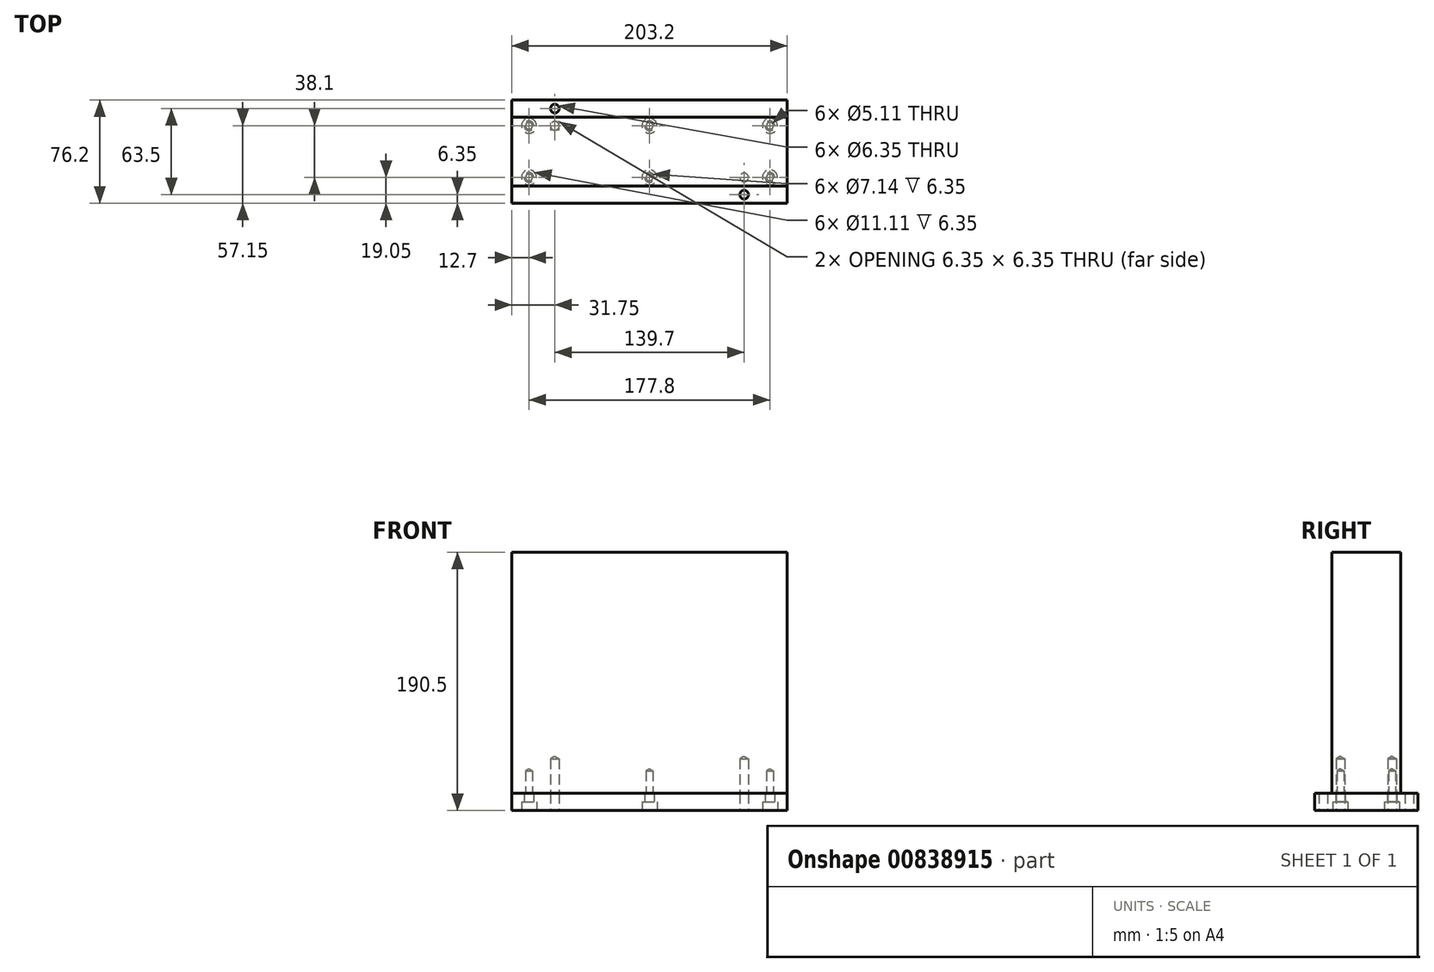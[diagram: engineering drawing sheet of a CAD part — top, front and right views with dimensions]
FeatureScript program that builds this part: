
annotation { "Feature Type Name" : "Feature", "Feature Type Description" : "" }
export const myFeature = defineFeature(function(context is Context, id is Id, definition is map)
    precondition{}
    {
        {
            var Q0;
            Q0=qCreatedBy(makeId("Top.planeOp"),FACE);
            var sketch = newSketch(context, id + "F0", { "sketchPlane" : qUnion([Q0])});
            skLineSegment(sketch, "E0.bottom", {"start": v(101.6, -38.1) * mm, "end": v(-101.6, -38.1) * mm});
            skLineSegment(sketch, "E0.top", {"start": v(101.6, 38.1) * mm, "end": v(-101.6, 38.1) * mm});
            skLineSegment(sketch, "E0.left", {"start": v(101.6, -38.1) * mm, "end": v(101.6, 38.1) * mm});
            skLineSegment(sketch, "E0.right", {"start": v(-101.6, -38.1) * mm, "end": v(-101.6, 38.1) * mm});
            skPoint(sketch, "E0.middle", {"position": v(0, 0) * mm});
            skSolve(sketch);
        }
        {
            var Q0;
            Q0=qSketchRegion(id+"F0",true);
            extrude(context, id + "F1", {"entities" : qUnion([Q0]), "depth" : 12.7 * mm, "offsetDistance" : 25.4 * mm});
        }
        {
            var Q0;
            Q0=makeQuery(id+"F1.opExtrude","CAP_FACE",FACE,{"disambiguationData":[OSD([sQuery(id+"F0.wireOp",EDGE,"E0.bottom"),sQuery(id+"F0.wireOp",EDGE,"E0.top"),sQuery(id+"F0.wireOp",EDGE,"E0.left"),sQuery(id+"F0.wireOp",EDGE,"E0.right")])],"isStart":false});
            var sketch = newSketch(context, id + "F2", { "sketchPlane" : qUnion([Q0])});
            skLineSegment(sketch, "E1.bottom", {"start": v(101.6, -25.4) * mm, "end": v(-101.6, -25.4) * mm});
            skLineSegment(sketch, "E1.top", {"start": v(101.6, 25.4) * mm, "end": v(-101.6, 25.4) * mm});
            skLineSegment(sketch, "E1.left", {"start": v(101.6, -25.4) * mm, "end": v(101.6, 25.4) * mm});
            skLineSegment(sketch, "E1.right", {"start": v(-101.6, -25.4) * mm, "end": v(-101.6, 25.4) * mm});
            skPoint(sketch, "E1.middle", {"position": v(0, 0) * mm});
            skSolve(sketch);
        }
        {
            var Q0;
            Q0=qSketchRegion(id+"F2",true);
            extrude(context, id + "F3", {"entities" : qUnion([Q0]), "depth" : 177.8 * mm, "offsetDistance" : 25.4 * mm});
        }
        {
            var Q0;
            Q0=makeQuery(id+"F1.opExtrude","CAP_FACE",FACE,{"disambiguationData":[OSD([sQuery(id+"F0.wireOp",EDGE,"E0.bottom"),sQuery(id+"F0.wireOp",EDGE,"E0.top"),sQuery(id+"F0.wireOp",EDGE,"E0.left"),sQuery(id+"F0.wireOp",EDGE,"E0.right")])],"isStart":true});
            var sketch = newSketch(context, id + "F4", { "sketchPlane" : qUnion([Q0])});
            skLineSegment(sketch, "E2.bottom", {"start": v(-88.9, 19.05) * mm, "end": v(88.9, 19.05) * mm, "construction": true});
            skLineSegment(sketch, "E2.top", {"start": v(-88.9, -19.05) * mm, "end": v(88.9, -19.05) * mm, "construction": true});
            skLineSegment(sketch, "E2.left", {"start": v(-88.9, 19.05) * mm, "end": v(-88.9, -19.05) * mm, "construction": true});
            skLineSegment(sketch, "E2.right", {"start": v(88.9, 19.05) * mm, "end": v(88.9, -19.05) * mm, "construction": true});
            skPoint(sketch, "E2.middle", {"position": v(0, 0) * mm});
            skPoint(sketch, "E3", {"position": v(0, 19.05) * mm});
            skPoint(sketch, "E4", {"position": v(0, -19.05) * mm});
            skPoint(sketch, "E5", {"position": v(69.85, 19.05) * mm});
            skPoint(sketch, "E6", {"position": v(-69.85, -19.05) * mm});
            skPoint(sketch, "E7", {"position": v(-69.85, -31.75) * mm});
            skPoint(sketch, "E8", {"position": v(69.85, 31.75) * mm});
            skSolve(sketch);
        }
        {
            var Q0;
            Q0=sQuery(id+"F4.wireOp",VERTEX,"E4");
            var Q1;
            Q1=sQuery(id+"F4.wireOp",VERTEX,"E3");
            var Q2;
            Q2=sQuery(id+"F4.wireOp",VERTEX,"E2.left.end");
            var Q3;
            Q3=sQuery(id+"F4.wireOp",VERTEX,"E2.left.start");
            var Q4;
            Q4=sQuery(id+"F4.wireOp",VERTEX,"E2.top.end");
            var Q5;
            Q5=sQuery(id+"F4.wireOp",VERTEX,"E2.bottom.end");
            var Q6;
            Q6=makeQuery(id+"F1.opExtrude","SWEPT_BODY",BODY,{"disambiguationData":[OSD([sQuery(id+"F0.wireOp",EDGE,"E0.bottom"),sQuery(id+"F0.wireOp",EDGE,"E0.top"),sQuery(id+"F0.wireOp",EDGE,"E0.left"),sQuery(id+"F0.wireOp",EDGE,"E0.right")])]});
            hole(context, id + "F5", {"style" : HoleStyle.C_BORE, "endStyle" : HoleEndStyle.THROUGH, "holeDiameter" : 7.14 * mm, "cBoreDiameter" : 11.1 * mm, "cBoreDepth" : 6.35 * mm, "majorDiameter" : 6.35 * mm, "isTappedThrough" : true, "tappedDepth" : 12.7 * mm, "tapClearance" : 3, "locations" : qUnion([Q0, Q1, Q2, Q3, Q4, Q5]), "scope" : qUnion([Q6])});
        }
        {
            var Q0;
            Q0=sQuery(id+"F4.wireOp",VERTEX,"E4");
            var Q1;
            Q1=sQuery(id+"F4.wireOp",VERTEX,"E3");
            var Q2;
            Q2=sQuery(id+"F4.wireOp",VERTEX,"E2.top.end");
            var Q3;
            Q3=sQuery(id+"F4.wireOp",VERTEX,"E2.bottom.end");
            var Q4;
            Q4=sQuery(id+"F4.wireOp",VERTEX,"E2.left.end");
            var Q5;
            Q5=sQuery(id+"F4.wireOp",VERTEX,"E2.left.start");
            var Q6;
            Q6=makeQuery(id+"F3.opExtrude","SWEPT_BODY",BODY,{"disambiguationData":[OSD([sQuery(id+"F2.wireOp",EDGE,"E1.bottom"),sQuery(id+"F2.wireOp",EDGE,"E1.top"),sQuery(id+"F2.wireOp",EDGE,"E1.left"),sQuery(id+"F2.wireOp",EDGE,"E1.right")])]});
            hole(context, id + "F6", {"style" : HoleStyle.SIMPLE, "endStyle" : HoleEndStyle.BLIND, "standardTappedOrClearance" : lookupTablePath({ "fit" : "Normal (ASME)", "standard" : "ANSI", "engagement" : "75%", "pitch" : "20 tpi", "size" : "1/4", "type" : "Tapped" }), "standardBlindInLast" : lookupTablePath({ "fit" : "Free", "standard" : "ANSI", "engagement" : "75%", "pitch" : "20 tpi", "size" : "1/4", "type" : "Tapped" }), "holeDiameter" : 5.1 * mm, "majorDiameter" : 6.35 * mm, "showTappedDepth" : true, "holeDepth" : 16.51 * mm, "isTappedThrough" : true, "tappedDepth" : 12.7 * mm, "tapClearance" : 3, "locations" : qUnion([Q0, Q1, Q2, Q3, Q4, Q5]), "scope" : qUnion([Q6])});
        }
        {
            var Q0;
            Q0=sQuery(id+"F4.wireOp",VERTEX,"E5");
            var Q1;
            Q1=sQuery(id+"F4.wireOp",VERTEX,"E6");
            var Q2;
            Q2=makeQuery(id+"F1.opExtrude","SWEPT_BODY",BODY,{"disambiguationData":[OSD([sQuery(id+"F0.wireOp",EDGE,"E0.bottom"),sQuery(id+"F0.wireOp",EDGE,"E0.top"),sQuery(id+"F0.wireOp",EDGE,"E0.left"),sQuery(id+"F0.wireOp",EDGE,"E0.right")])]});
            var Q3;
            Q3=makeQuery(id+"F3.opExtrude","SWEPT_BODY",BODY,{"disambiguationData":[OSD([sQuery(id+"F2.wireOp",EDGE,"E1.bottom"),sQuery(id+"F2.wireOp",EDGE,"E1.top"),sQuery(id+"F2.wireOp",EDGE,"E1.left"),sQuery(id+"F2.wireOp",EDGE,"E1.right")])]});
            hole(context, id + "F7", {"style" : HoleStyle.SIMPLE, "endStyle" : HoleEndStyle.BLIND_IN_LAST, "holeDiameter" : 6.35 * mm, "tapDrillDiameter" : 6.35 * mm, "majorDiameter" : 6.35 * mm, "holeDepth" : 25.4 * mm, "isTappedThrough" : true, "tappedDepth" : 12.7 * mm, "tapClearance" : 3, "locations" : qUnion([Q0, Q1]), "scope" : qUnion([Q2, Q3])});
        }
        {
            var Q0;
            Q0=sQuery(id+"F4.wireOp",VERTEX,"E7");
            var Q1;
            Q1=sQuery(id+"F4.wireOp",VERTEX,"E8");
            var Q2;
            Q2=makeQuery(id+"F1.opExtrude","SWEPT_BODY",BODY,{"disambiguationData":[OSD([sQuery(id+"F0.wireOp",EDGE,"E0.bottom"),sQuery(id+"F0.wireOp",EDGE,"E0.top"),sQuery(id+"F0.wireOp",EDGE,"E0.left"),sQuery(id+"F0.wireOp",EDGE,"E0.right")])]});
            hole(context, id + "F8", {"style" : HoleStyle.SIMPLE, "endStyle" : HoleEndStyle.THROUGH, "holeDiameter" : 6.35 * mm, "majorDiameter" : 6.35 * mm, "isTappedThrough" : true, "tappedDepth" : 12.7 * mm, "tapClearance" : 3, "locations" : qUnion([Q0, Q1]), "scope" : qUnion([Q2])});
        }
    });
